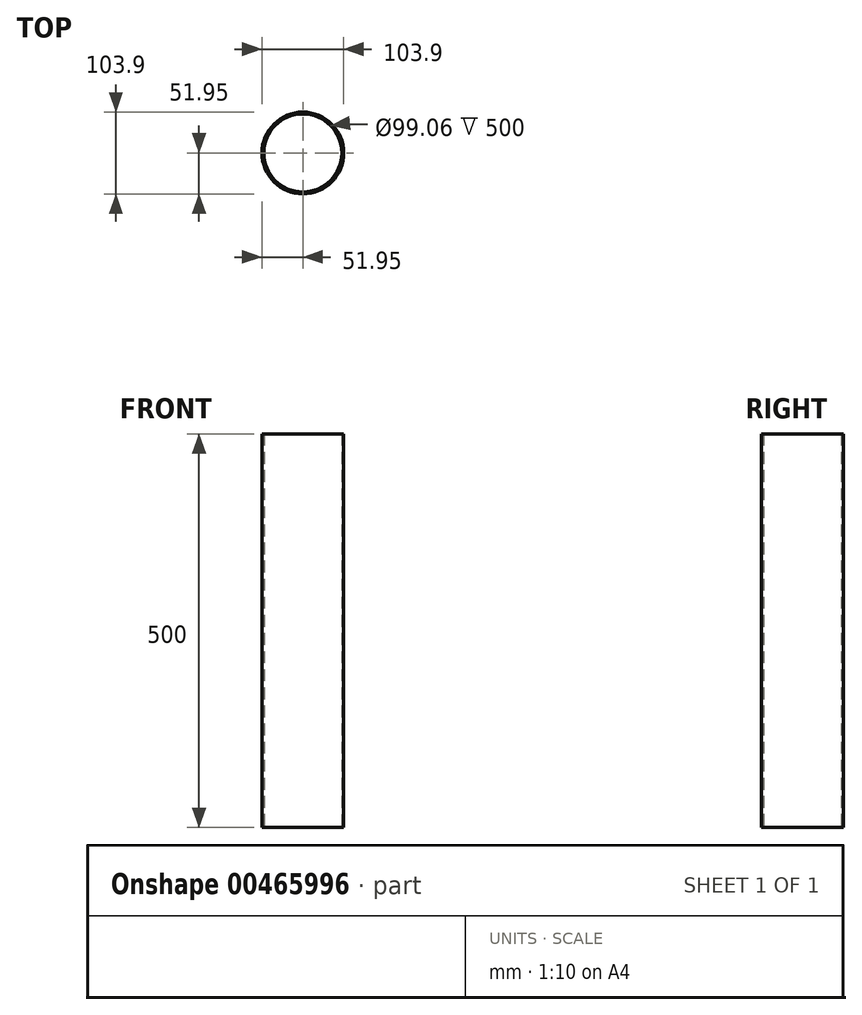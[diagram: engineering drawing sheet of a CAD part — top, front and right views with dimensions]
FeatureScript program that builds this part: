
annotation { "Feature Type Name" : "Feature", "Feature Type Description" : "" }
export const myFeature = defineFeature(function(context is Context, id is Id, definition is map)
    precondition{}
    {
        {
            var Q0;
            Q0=qCreatedBy(makeId("Top.planeOp"),FACE);
            var sketch = newSketch(context, id + "F0", { "sketchPlane" : qUnion([Q0])});
            skCircle(sketch, "E0", {"center": v(0, 0) * mm, "radius": 49.53 * mm});
            skCircle(sketch, "E1", {"center": v(0, 0) * mm, "radius": 51.95 * mm});
            skSolve(sketch);
        }
        {
            var Q0;
            Q0 = qSketchRegion(id + "F0", true);
            extrude(context, id + "F1", {"entities" : qUnion([Q0]), "depth" : 500 * mm, "offsetDistance" : 25 * mm});
        }
    });
